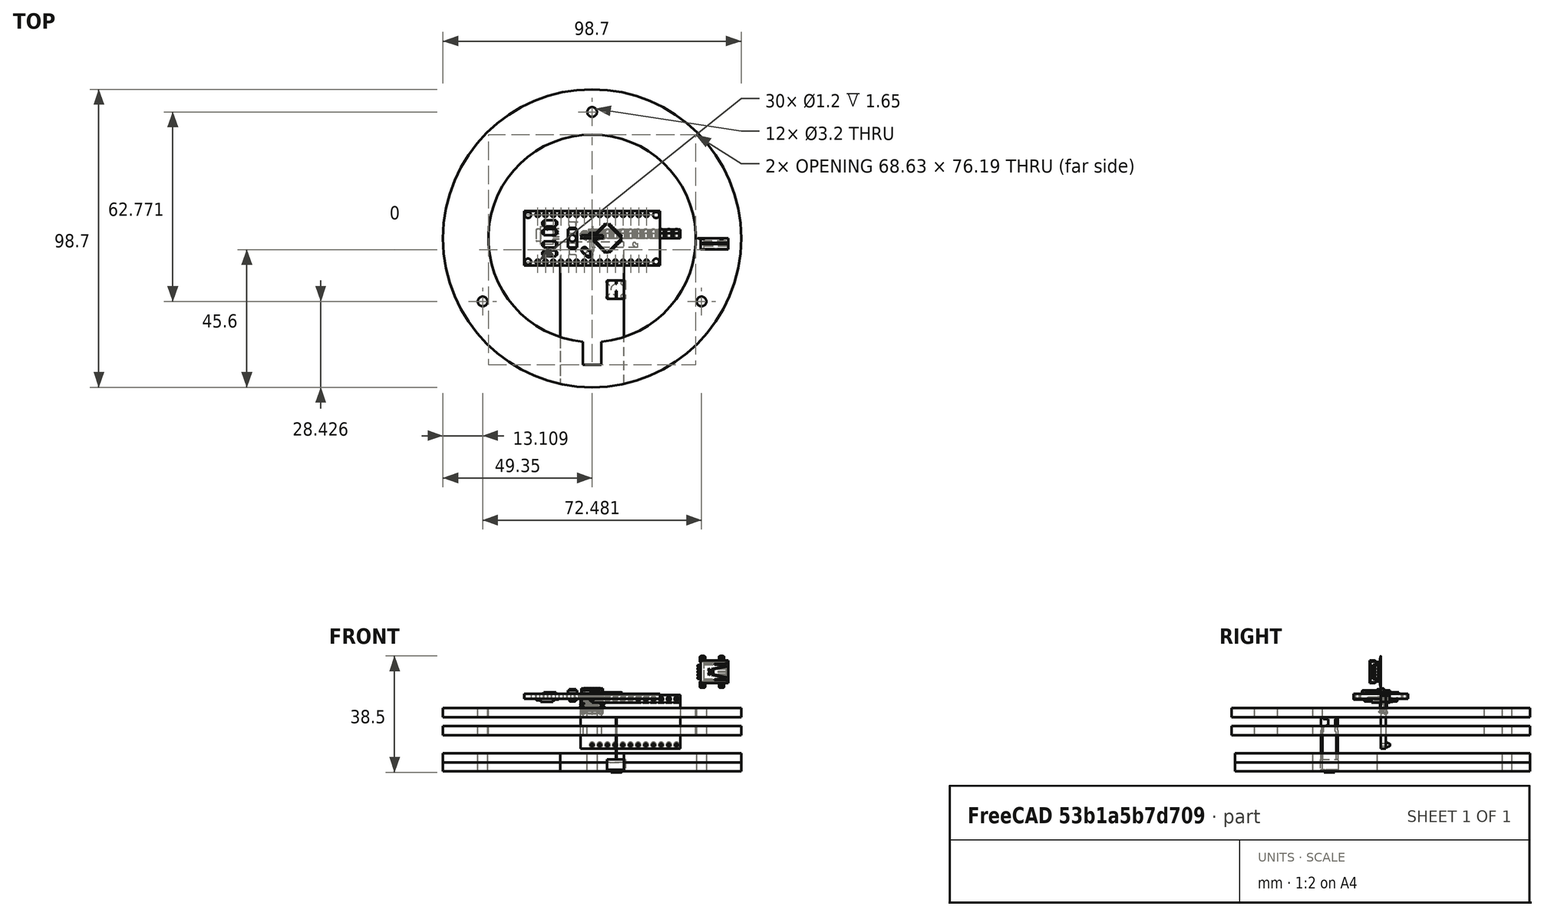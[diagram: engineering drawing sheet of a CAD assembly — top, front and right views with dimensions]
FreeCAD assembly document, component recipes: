
FREECAD ASSEMBLY — COMPONENT RECIPES ("infinity_01")

This assembly document has 81 components, labeled P0..P80 below (a component is one placed body or linked part). 6 of them carry a construction recipe — the FreeCAD feature program that regenerates the part from scratch, quoted from this document or its linked companion documents; the rest are supplied as boundary geometry only. No exploded tour is included for this assembly.
COMPONENT P0 — recipe-attached ("front_mirror_50%", modeled in this document).
Construction recipe (the document's own serialized feature program — sketch geometry with constraints, then the solid features built on it; lengths are millimeters unless a unit is written):

FEATURE [Sketcher::SketchObject] Sketch
  FullyConstrained = true
  MapMode = 5
  Support = -> [XY_Plane]
  expr: Constraints[18] = Spreadsheet.length_of_LEDS / 3.14 + 5mm + 15mm
  expr: Constraints[2] = Spreadsheet.length_of_LEDS / 3.14 + 5mm + 30mm
  expr: Constraints[3] = Spreadsheet.screw_hole_dia + 0.2mm
  sketch-geometry (8):
    g0: Circle CenterX=0 CenterY=0 CenterZ=0 NormalX=0 NormalY=0 NormalZ=1 AngleXU=0 Radius=49.3471
    g1: Circle CenterX=-36.2407 CenterY=-20.9236 CenterZ=0 NormalX=0 NormalY=0 NormalZ=1 AngleXU=0 Radius=1.6
    g2: Circle CenterX=36.2407 CenterY=-20.9236 CenterZ=0 NormalX=0 NormalY=0 NormalZ=1 AngleXU=0 Radius=1.6
    g3: Circle CenterX=0 CenterY=41.8471 CenterZ=0 NormalX=0 NormalY=0 NormalZ=1 AngleXU=0 Radius=1.6
    g4: LineSegment StartX=0 StartY=0 StartZ=0 EndX=0 EndY=41.8471 EndZ=0
    g5: LineSegment StartX=0 StartY=0 StartZ=0 EndX=36.2407 EndY=-20.9236 EndZ=0
    g6: LineSegment StartX=0 StartY=0 StartZ=0 EndX=-36.2407 EndY=-20.9236 EndZ=0
    g7: Circle CenterX=0 CenterY=0 CenterZ=0 NormalX=0 NormalY=0 NormalZ=1 AngleXU=0 Radius=41.8471
  constraints (19):
    c: Coincident(g0,g-1)
    c: PointOnObject(g3,g-2)
    c: Diameter(g0) = 98.6943
    c: Diameter(g1) = 3.2
    c: Equal(g1,g3)
    c: Equal(g1,g2)
    c: Coincident(g4,g0)
    c: Coincident(g4,g3)
    c: Coincident(g5,g0)
    c: Coincident(g5,g2)
    c: Coincident(g6,g0)
    c: Coincident(g6,g1)
    c: Equal(g6,g5)
    c: Equal(g5,g4)
    c: Angle(g5,g4) = 2.0944
    c: Angle(g4,g6) = 2.0944
    c: Coincident(g7,g0)
    c: PointOnObject(g3,g7)
    c: Diameter(g7) = 83.6943
FEATURE [PartDesign::Pad] Pad
  Direction = (1,1,1)
  Length = 3
  Length2 = 100
  Profile = -> Sketch
  Type = 0
FEATURE [PartDesign::Body] Body  label="front_mirror_50%"
  Group = -> [Sketch,Pad]
  Origin = -> Origin
  Tip = -> Pad
COMPONENT P1 — recipe-attached ("spacer01", modeled in this document).
Construction recipe (the document's own serialized feature program — sketch geometry with constraints, then the solid features built on it; lengths are millimeters unless a unit is written):

FEATURE [PartDesign::SubShapeBinder] Binder
  BindMode = 0
  ClaimChildren = false
  Context = -> Body001 [Binder.]
  Fuse = false
  MakeFace = true
  PartialLoad = false
  Relative = true
  Support = -> [Body]
  _Version = 2
FEATURE [Sketcher::SketchObject] Sketch001
  ExternalGeometry = -> [Binder]
  FullyConstrained = true
  MapMode = 5
  Placement = pos=(0,0,0) rot=(1,0,0;3.14159rad)
  Support = -> [Binder]
  expr: Constraints[8] = Spreadsheet.length_of_LEDS / 3.14 + 5mm
  sketch-geometry (10):
    g0: Circle CenterX=0 CenterY=0 CenterZ=0 NormalX=0 NormalY=0 NormalZ=1 AngleXU=0 Radius=49.3471
    g1: Circle CenterX=-36.2407 CenterY=20.9236 CenterZ=0 NormalX=0 NormalY=0 NormalZ=1 AngleXU=0 Radius=1.6
    g2: Circle CenterX=36.2407 CenterY=20.9236 CenterZ=0 NormalX=0 NormalY=0 NormalZ=1 AngleXU=0 Radius=1.6
    g3: Circle CenterX=0 CenterY=-41.8471 CenterZ=0 NormalX=0 NormalY=0 NormalZ=1 AngleXU=0 Radius=1.6
    g4: ArcOfCircle CenterX=0 CenterY=0 CenterZ=0 NormalX=0 NormalY=0 NormalZ=1 AngleXU=0 Radius=34.3471 StartAngle=1.65825 EndAngle=7.76653
    g5: LineSegment StartX=-3 StartY=41.8471 StartZ=0 EndX=3 EndY=41.8471 EndZ=0
    g6: LineSegment StartX=3 StartY=41.8471 StartZ=0 EndX=3 EndY=34.2159 EndZ=0
    g7: LineSegment StartX=-3 StartY=34.2159 StartZ=0 EndX=-3 EndY=41.8471 EndZ=0
    g8: LineSegment StartX=0 StartY=0 StartZ=0 EndX=-36.2407 EndY=20.9236 EndZ=0
    g9: LineSegment StartX=0 StartY=0 StartZ=0 EndX=0 EndY=41.8471 EndZ=0
  constraints (24):
    c: Coincident(g0,g-1)
    c: Coincident(g1,g-4)
    c: Coincident(g2,g-5)
    c: Coincident(g3,g-6)
    c: Equal(g3,g-6)
    c: Equal(g-4,g1)
    c: Equal(g-5,g2)
    c: Coincident(g4,g0)
    c: Diameter(g4) = 68.6943
    c: Coincident(g5,g6)
    c: Coincident(g7,g5)
    c: Vertical(g6)
    c: Vertical(g7)
    c: Symmetric(g5,g5,g-2)
    c: DistanceX(g5,g5) = 6
    c: Coincident(g4,g7)
    c: Coincident(g4,g6)
    c: Equal(g0,g-3)
    c: Coincident(g8,g0)
    c: Coincident(g8,g1)
    c: Coincident(g9,g0)
    c: PointOnObject(g9,g5)
    c: Vertical(g9)
    c: Equal(g8,g9)
FEATURE [PartDesign::Pad] Pad001
  Direction = (1,1,1)
  Length = 3
  Length2 = 100
  Profile = -> Sketch001
  Type = 0
FEATURE [PartDesign::Body] Body001  label="spacer01"
  Group = -> [Binder,Sketch001,Pad001]
  Origin = -> Origin001
  Tip = -> Pad001
COMPONENT P2 — recipe-attached ("bezel", modeled in this document).
Construction recipe (the document's own serialized feature program — sketch geometry with constraints, then the solid features built on it; lengths are millimeters unless a unit is written):

FEATURE [PartDesign::SubShapeBinder] Binder001
  BindMode = 0
  ClaimChildren = false
  Context = -> Body002 [Binder001.]
  Fuse = false
  MakeFace = true
  PartialLoad = false
  Relative = true
  Support = -> [Body]
  _Version = 2
FEATURE [PartDesign::SubShapeBinder] Binder002
  BindMode = 0
  ClaimChildren = false
  Context = -> Body002 [Binder002.]
  Fuse = false
  MakeFace = true
  PartialLoad = false
  Relative = true
  Support = -> [Body001]
  _Version = 2
FEATURE [Sketcher::SketchObject] Sketch002
  ExternalGeometry = -> [Binder001,Binder002]
  FullyConstrained = true
  MapMode = 5
  Placement = pos=(0,0,3) rot=(0,0,1;0rad)
  Support = -> [Binder001]
  expr: Constraints[9] = Spreadsheet.length_of_LEDS / 3.14
  sketch-geometry (5):
    g0: Circle CenterX=0 CenterY=0 CenterZ=0 NormalX=0 NormalY=0 NormalZ=1 AngleXU=0 Radius=49.3471
    g1: Circle CenterX=0 CenterY=0 CenterZ=0 NormalX=0 NormalY=0 NormalZ=1 AngleXU=0 Radius=31.8471
    g2: Circle CenterX=-36.2407 CenterY=-20.9236 CenterZ=0 NormalX=0 NormalY=0 NormalZ=1 AngleXU=0 Radius=1.6
    g3: Circle CenterX=0 CenterY=41.8471 CenterZ=0 NormalX=0 NormalY=0 NormalZ=1 AngleXU=0 Radius=1.6
    g4: Circle CenterX=36.2407 CenterY=-20.9236 CenterZ=0 NormalX=0 NormalY=0 NormalZ=1 AngleXU=0 Radius=1.6
  constraints (10):
    c: Coincident(g0,g-1)
    c: Coincident(g1,g0)
    c: Coincident(g2,g-6)
    c: Coincident(g3,g-4)
    c: Coincident(g4,g-5)
    c: Equal(g-5,g4)
    c: Equal(g2,g-6)
    c: Equal(g-4,g3)
    c: Equal(g0,g-3)
    c: Diameter(g1) = 63.6943
FEATURE [PartDesign::Pad] Pad002
  Direction = (1,1,1)
  Length = 3
  Length2 = 100
  Profile = -> Sketch002
  Type = 0
FEATURE [PartDesign::Body] Body002  label="bezel"
  Group = -> [Binder001,Sketch002,Binder002,Pad002]
  Origin = -> Origin002
  Tip = -> Pad002
COMPONENT P3 — geometry summary ("spacer02"; no construction recipe available for this part):
  bounding box: 98.7 x 98.7 x 3.0 mm
  tessellated surface: 2,532 triangles
  volume: 11624 mm^3 (40% of its bounding box)
  symmetry: 2-fold rotationally symmetric about the y axis; mirror-symmetric across its x mid-plane, z mid-plane
COMPONENT P4 — geometry summary ("spacer03"; no construction recipe available for this part):
  bounding box: 98.7 x 98.7 x 3.0 mm
  tessellated surface: 2,532 triangles
  volume: 11624 mm^3 (40% of its bounding box)
  symmetry: 2-fold rotationally symmetric about the y axis; mirror-symmetric across its x mid-plane, z mid-plane
COMPONENT P5 — recipe-attached ("back_mirror_100%", modeled in this document).
Construction recipe (the document's own serialized feature program — sketch geometry with constraints, then the solid features built on it; lengths are millimeters unless a unit is written):

FEATURE [PartDesign::SubShapeBinder] Binder007
  BindMode = 0
  ClaimChildren = false
  Context = -> Body005 [Binder007.]
  Fuse = false
  MakeFace = true
  PartialLoad = false
  Relative = true
  Support = -> [Body009]
  _Version = 2
FEATURE [Sketcher::SketchObject] Sketch003
  ExternalGeometry = -> [Binder007]
  FullyConstrained = true
  MapMode = 5
  Placement = pos=(0,0,-6) rot=(1,0,0;3.14159rad)
  Support = -> [Binder007]
  sketch-geometry (8):
    g0: Circle CenterX=0 CenterY=0 CenterZ=0 NormalX=0 NormalY=0 NormalZ=1 AngleXU=0 Radius=49.3471
    g1: Circle CenterX=-36.2407 CenterY=20.9236 CenterZ=0 NormalX=0 NormalY=0 NormalZ=1 AngleXU=0 Radius=1.6
    g2: Circle CenterX=36.2407 CenterY=20.9236 CenterZ=0 NormalX=0 NormalY=0 NormalZ=1 AngleXU=0 Radius=1.6
    g3: Circle CenterX=0 CenterY=-41.8471 CenterZ=0 NormalX=0 NormalY=0 NormalZ=1 AngleXU=0 Radius=1.6
    g4: LineSegment StartX=3 StartY=34.2159 StartZ=0 EndX=-3 EndY=34.2159 EndZ=0
    g5: LineSegment StartX=-3 StartY=34.2159 StartZ=0 EndX=-3 EndY=41.8471 EndZ=0
    g6: LineSegment StartX=-3 StartY=41.8471 StartZ=0 EndX=3 EndY=41.8471 EndZ=0
    g7: LineSegment StartX=3 StartY=41.8471 StartZ=0 EndX=3 EndY=34.2159 EndZ=0
  constraints (18):
    c: Coincident(g0,g-1)
    c: Coincident(g4,g5)
    c: Coincident(g5,g6)
    c: Coincident(g6,g7)
    c: Coincident(g7,g4)
    c: Horizontal(g4)
    c: Horizontal(g6)
    c: Vertical(g5)
    c: Vertical(g7)
    c: Equal(g-3,g0)
    c: Equal(g-4,g1)
    c: Coincident(g1,g-4)
    c: Coincident(g2,g-5)
    c: Equal(g-5,g2)
    c: Coincident(g3,g-6)
    c: Equal(g-6,g3)
    c: Coincident(g5,g-7)
    c: Coincident(g4,g-8)
FEATURE [PartDesign::Pad] Pad003
  Direction = (1,1,1)
  Length = 3
  Length2 = 100
  Profile = -> Sketch003
  Type = 0
FEATURE [PartDesign::Body] Body005  label="back_mirror_100%"
  Group = -> [Sketch003,Pad003,Binder007]
  Origin = -> Origin005
  Placement = pos=(0,0,-6) rot=(0,0,1;0rad)
  Tip = -> Pad003
COMPONENT P6 — recipe-attached ("arduino_micro_back001", modeled in this document).
Construction recipe (the document's own serialized feature program — sketch geometry with constraints, then the solid features built on it; lengths are millimeters unless a unit is written):

FEATURE [PartDesign::SubShapeBinder] Binder004
  BindMode = 0
  ClaimChildren = false
  Context = -> Body006 [Binder004.]
  Fuse = false
  MakeFace = true
  PartialLoad = false
  Relative = true
  Support = -> [Body005]
  _Version = 2
FEATURE [Sketcher::SketchObject] Sketch004
  ExternalGeometry = -> [Binder004]
  FullyConstrained = true
  MapMode = 5
  Placement = pos=(0,0,-15) rot=(1,0,0;3.14159rad)
  Support = -> [Binder004]
  expr: Constraints[6] = Spreadsheet.width
  expr: Constraints[9] = Spreadsheet.Length
  sketch-geometry (7):
    g0: ArcOfCircle CenterX=0 CenterY=0 CenterZ=0 NormalX=0 NormalY=0 NormalZ=1 AngleXU=0 Radius=49.3471 StartAngle=1.78521 EndAngle=7.63956
    g1: LineSegment StartX=10.5 StartY=48.2171 StartZ=0 EndX=10.5 EndY=1.21711 EndZ=0
    g2: LineSegment StartX=10.5 StartY=1.21711 StartZ=0 EndX=-10.5 EndY=1.21711 EndZ=0
    g3: LineSegment StartX=-10.5 StartY=1.21711 StartZ=0 EndX=-10.5 EndY=48.2171 EndZ=0
    g4: Circle CenterX=-36.2407 CenterY=20.9236 CenterZ=0 NormalX=0 NormalY=0 NormalZ=1 AngleXU=0 Radius=1.6
    g5: Circle CenterX=36.2407 CenterY=20.9236 CenterZ=0 NormalX=0 NormalY=0 NormalZ=1 AngleXU=0 Radius=1.6
    g6: Circle CenterX=0 CenterY=-41.8471 CenterZ=0 NormalX=0 NormalY=0 NormalZ=1 AngleXU=0 Radius=1.6
  constraints (17):
    c: Coincident(g0,g-1)
    c: Coincident(g1,g2)
    c: Coincident(g2,g3)
    c: Vertical(g1)
    c: Vertical(g3)
    c: Symmetric(g2,g1,g-2)
    c: DistanceX(g2,g2) = 21
    c: Coincident(g0,g3)
    c: Coincident(g0,g1)
    c: Distance(g3) = 47
    c: Equal(g0,g-3)
    c: Coincident(g4,g-4)
    c: Coincident(g5,g-5)
    c: Coincident(g6,g-6)
    c: Equal(g6,g-6)
    c: Equal(g-4,g4)
    c: Equal(g-5,g5)
FEATURE [PartDesign::Pad] Pad004
  Direction = (1,1,1)
  Length = 3
  Length2 = 100
  Profile = -> Sketch004
  Type = 0
FEATURE [PartDesign::Body] Body006  label="arduino_micro_back001"
  Group = -> [Binder004,Sketch004,Pad004]
  Origin = -> Origin006
  Tip = -> Pad004
COMPONENT P7 — geometry summary ("arduino_micro_back002"; no construction recipe available for this part):
  bounding box: 98.7 x 97.6 x 3.0 mm
  tessellated surface: 2,004 triangles
  volume: 19870 mm^3 (69% of its bounding box)
  symmetry: mirror-symmetric across its x mid-plane, z mid-plane
COMPONENT P8 — geometry summary ("spacer04"; no construction recipe available for this part):
  bounding box: 98.7 x 98.7 x 3.0 mm
  tessellated surface: 2,532 triangles
  volume: 11624 mm^3 (40% of its bounding box)
  symmetry: 2-fold rotationally symmetric about the y axis; mirror-symmetric across its x mid-plane, z mid-plane
COMPONENT P9 — geometry summary ("arduino_micro_back003"; no construction recipe available for this part):
  bounding box: 98.7 x 97.6 x 3.0 mm
  tessellated surface: 2,004 triangles
  volume: 19870 mm^3 (69% of its bounding box)
  symmetry: mirror-symmetric across its x mid-plane, z mid-plane
COMPONENT P10 — recipe-attached ("back", modeled in this document).
Construction recipe (the document's own serialized feature program — sketch geometry with constraints, then the solid features built on it; lengths are millimeters unless a unit is written):

FEATURE [PartDesign::SubShapeBinder] Binder005
  BindMode = 0
  ClaimChildren = false
  Context = -> Body011 [Binder005.]
  Fuse = false
  MakeFace = true
  PartialLoad = false
  Relative = true
  Support = -> [Body010]
  _Version = 2
FEATURE [PartDesign::SubShapeBinder] Binder006
  BindMode = 0
  ClaimChildren = false
  Context = -> Body011 [Binder006.]
  Fuse = false
  MakeFace = true
  PartialLoad = false
  Relative = true
  Support = -> [Solid105]
  _Version = 2
FEATURE [Sketcher::SketchObject] Sketch005
  ExternalGeometry = -> [Binder005,Binder006]
  FullyConstrained = true
  MapMode = 5
  Placement = pos=(0,0,-24) rot=(1,0,0;3.14159rad)
  Support = -> [Binder005]
  sketch-geometry (5):
    g0: Circle CenterX=0 CenterY=0 CenterZ=0 NormalX=0 NormalY=0 NormalZ=1 AngleXU=0 Radius=49.3471
    g1: Circle CenterX=-36.2407 CenterY=20.9236 CenterZ=0 NormalX=0 NormalY=0 NormalZ=1 AngleXU=0 Radius=1.6
    g2: Circle CenterX=36.2407 CenterY=20.9236 CenterZ=0 NormalX=0 NormalY=0 NormalZ=1 AngleXU=0 Radius=1.6
    g3: Circle CenterX=0 CenterY=-41.8471 CenterZ=0 NormalX=0 NormalY=0 NormalZ=1 AngleXU=0 Radius=1.6
    g4: Circle CenterX=8 CenterY=17 CenterZ=0 NormalX=0 NormalY=0 NormalZ=1 AngleXU=0 Radius=5
  constraints (10):
    c: Coincident(g0,g-1)
    c: Coincident(g2,g-5)
    c: Coincident(g3,g-6)
    c: Equal(g-6,g3)
    c: Equal(g1,g-4)
    c: Coincident(g1,g-4)
    c: Equal(g-5,g2)
    c: Equal(g0,g-3)
    c: Coincident(g-7,g4)
    c: Diameter(g4) = 10
FEATURE [PartDesign::Pad] Pad005
  Direction = (1,1,1)
  Length = 3
  Length2 = 100
  Profile = -> Sketch005
  Type = 0
FEATURE [PartDesign::Body] Body011  label="back"
  Group = -> [Binder005,Sketch005,Binder006,Pad005]
  Origin = -> Origin011
  Tip = -> Pad005
COMPONENT P11 — geometry summary ("Component3:2"; no construction recipe available for this part):
  bounding box: 0.9 x 0.6 x 0.3 mm
  tessellated surface: 80 triangles
  volume: 0 mm^3 (64% of its bounding box)
  symmetry: mirror-symmetric across its x mid-plane
COMPONENT P12 — geometry summary ("Component3:3"; no construction recipe available for this part):
  bounding box: 0.9 x 0.6 x 0.3 mm
  tessellated surface: 80 triangles
  volume: 0 mm^3 (64% of its bounding box)
  symmetry: mirror-symmetric across its x mid-plane
COMPONENT P13 — geometry summary ("Component3:4"; no construction recipe available for this part):
  bounding box: 0.9 x 0.6 x 0.3 mm
  tessellated surface: 80 triangles
  volume: 0 mm^3 (64% of its bounding box)
  symmetry: mirror-symmetric across its x mid-plane
COMPONENT P14 — geometry summary ("Component3:5"; no construction recipe available for this part):
  bounding box: 0.9 x 0.6 x 0.3 mm
  tessellated surface: 80 triangles
  volume: 0 mm^3 (64% of its bounding box)
  symmetry: mirror-symmetric across its x mid-plane
COMPONENT P15 — geometry summary ("Component3:6"; no construction recipe available for this part):
  bounding box: 0.9 x 0.6 x 0.3 mm
  tessellated surface: 80 triangles
  volume: 0 mm^3 (64% of its bounding box)
  symmetry: mirror-symmetric across its x mid-plane
COMPONENT P16 — geometry summary ("Component3:7"; no construction recipe available for this part):
  bounding box: 0.9 x 0.6 x 0.3 mm
  tessellated surface: 80 triangles
  volume: 0 mm^3 (64% of its bounding box)
  symmetry: mirror-symmetric across its x mid-plane
COMPONENT P17 — geometry summary ("Component3:8"; no construction recipe available for this part):
  bounding box: 0.9 x 0.6 x 0.3 mm
  tessellated surface: 80 triangles
  volume: 0 mm^3 (64% of its bounding box)
  symmetry: mirror-symmetric across its x mid-plane
COMPONENT P18 — geometry summary ("Component3:9"; no construction recipe available for this part):
  bounding box: 0.9 x 0.6 x 0.3 mm
  tessellated surface: 80 triangles
  volume: 0 mm^3 (64% of its bounding box)
  symmetry: mirror-symmetric across its x mid-plane
COMPONENT P19 — geometry summary ("Component3:10"; no construction recipe available for this part):
  bounding box: 0.9 x 0.6 x 0.3 mm
  tessellated surface: 80 triangles
  volume: 0 mm^3 (64% of its bounding box)
  symmetry: mirror-symmetric across its x mid-plane
COMPONENT P20 — geometry summary ("Component3:11"; no construction recipe available for this part):
  bounding box: 0.9 x 0.6 x 0.3 mm
  tessellated surface: 80 triangles
  volume: 0 mm^3 (64% of its bounding box)
  symmetry: mirror-symmetric across its x mid-plane
COMPONENT P21 — geometry summary ("Component3:12"; no construction recipe available for this part):
  bounding box: 0.9 x 0.6 x 0.3 mm
  tessellated surface: 80 triangles
  volume: 0 mm^3 (64% of its bounding box)
  symmetry: mirror-symmetric across its x mid-plane
COMPONENT P22 — geometry summary ("Component3:13"; no construction recipe available for this part):
  bounding box: 0.9 x 0.6 x 0.3 mm
  tessellated surface: 80 triangles
  volume: 0 mm^3 (64% of its bounding box)
  symmetry: mirror-symmetric across its x mid-plane
COMPONENT P23 — geometry summary ("Component3:14"; no construction recipe available for this part):
  bounding box: 0.9 x 0.6 x 0.3 mm
  tessellated surface: 80 triangles
  volume: 0 mm^3 (64% of its bounding box)
  symmetry: mirror-symmetric across its x mid-plane
COMPONENT P24 — geometry summary ("Component3:15"; no construction recipe available for this part):
  bounding box: 0.9 x 0.6 x 0.3 mm
  tessellated surface: 80 triangles
  volume: 0 mm^3 (64% of its bounding box)
  symmetry: mirror-symmetric across its x mid-plane
COMPONENT P25 — geometry summary ("Component3:16"; no construction recipe available for this part):
  bounding box: 0.9 x 0.6 x 0.3 mm
  tessellated surface: 80 triangles
  volume: 0 mm^3 (64% of its bounding box)
  symmetry: mirror-symmetric across its x mid-plane
COMPONENT P26 — geometry summary ("Component3(Mirror):2"; no construction recipe available for this part):
  bounding box: 0.9 x 0.6 x 0.3 mm
  tessellated surface: 80 triangles
  volume: 0 mm^3 (64% of its bounding box)
  symmetry: mirror-symmetric across its x mid-plane
COMPONENT P27 — geometry summary ("Component3(Mirror):3"; no construction recipe available for this part):
  bounding box: 0.9 x 0.6 x 0.3 mm
  tessellated surface: 80 triangles
  volume: 0 mm^3 (64% of its bounding box)
  symmetry: mirror-symmetric across its x mid-plane
COMPONENT P28 — geometry summary ("Component3(Mirror):4"; no construction recipe available for this part):
  bounding box: 0.9 x 0.6 x 0.3 mm
  tessellated surface: 80 triangles
  volume: 0 mm^3 (64% of its bounding box)
  symmetry: mirror-symmetric across its x mid-plane
COMPONENT P29 — geometry summary ("Component3(Mirror):5"; no construction recipe available for this part):
  bounding box: 0.9 x 0.6 x 0.3 mm
  tessellated surface: 80 triangles
  volume: 0 mm^3 (64% of its bounding box)
  symmetry: mirror-symmetric across its x mid-plane
COMPONENT P30 — geometry summary ("Component3(Mirror):6"; no construction recipe available for this part):
  bounding box: 0.9 x 0.6 x 0.3 mm
  tessellated surface: 80 triangles
  volume: 0 mm^3 (64% of its bounding box)
  symmetry: mirror-symmetric across its x mid-plane
COMPONENT P31 — geometry summary ("Component3(Mirror):7"; no construction recipe available for this part):
  bounding box: 0.9 x 0.6 x 0.3 mm
  tessellated surface: 80 triangles
  volume: 0 mm^3 (64% of its bounding box)
  symmetry: mirror-symmetric across its x mid-plane
COMPONENT P32 — geometry summary ("Component3(Mirror):8"; no construction recipe available for this part):
  bounding box: 0.9 x 0.6 x 0.3 mm
  tessellated surface: 80 triangles
  volume: 0 mm^3 (64% of its bounding box)
  symmetry: mirror-symmetric across its x mid-plane
COMPONENT P33 — geometry summary ("Component3(Mirror):9"; no construction recipe available for this part):
  bounding box: 0.9 x 0.6 x 0.3 mm
  tessellated surface: 80 triangles
  volume: 0 mm^3 (64% of its bounding box)
  symmetry: mirror-symmetric across its x mid-plane
COMPONENT P34 — geometry summary ("Component3(Mirror):10"; no construction recipe available for this part):
  bounding box: 0.9 x 0.6 x 0.3 mm
  tessellated surface: 80 triangles
  volume: 0 mm^3 (64% of its bounding box)
  symmetry: mirror-symmetric across its x mid-plane
COMPONENT P35 — geometry summary ("Component3(Mirror):11"; no construction recipe available for this part):
  bounding box: 0.9 x 0.6 x 0.3 mm
  tessellated surface: 80 triangles
  volume: 0 mm^3 (64% of its bounding box)
  symmetry: mirror-symmetric across its x mid-plane
COMPONENT P36 — geometry summary ("Component3(Mirror):12"; no construction recipe available for this part):
  bounding box: 0.9 x 0.6 x 0.3 mm
  tessellated surface: 80 triangles
  volume: 0 mm^3 (64% of its bounding box)
  symmetry: mirror-symmetric across its x mid-plane
COMPONENT P37 — geometry summary ("Component3(Mirror):13"; no construction recipe available for this part):
  bounding box: 0.9 x 0.6 x 0.3 mm
  tessellated surface: 80 triangles
  volume: 0 mm^3 (64% of its bounding box)
  symmetry: mirror-symmetric across its x mid-plane
COMPONENT P38 — geometry summary ("Component3(Mirror):14"; no construction recipe available for this part):
  bounding box: 0.9 x 0.6 x 0.3 mm
  tessellated surface: 80 triangles
  volume: 0 mm^3 (64% of its bounding box)
  symmetry: mirror-symmetric across its x mid-plane
COMPONENT P39 — geometry summary ("Component3(Mirror):15"; no construction recipe available for this part):
  bounding box: 0.9 x 0.6 x 0.3 mm
  tessellated surface: 80 triangles
  volume: 0 mm^3 (64% of its bounding box)
  symmetry: mirror-symmetric across its x mid-plane
COMPONENT P40 — geometry summary ("Component3(Mirror):16"; no construction recipe available for this part):
  bounding box: 0.9 x 0.6 x 0.3 mm
  tessellated surface: 80 triangles
  volume: 0 mm^3 (64% of its bounding box)
  symmetry: mirror-symmetric across its x mid-plane
COMPONENT P41 — geometry summary ("Component5:3"; no construction recipe available for this part):
  bounding box: 0.7 x 0.5 x 0.2 mm
  tessellated surface: 76 triangles
  volume: 0 mm^3 (64% of its bounding box)
  symmetry: mirror-symmetric across its y mid-plane
COMPONENT P42 — geometry summary ("Component5:4"; no construction recipe available for this part):
  bounding box: 0.7 x 0.5 x 0.2 mm
  tessellated surface: 76 triangles
  volume: 0 mm^3 (64% of its bounding box)
  symmetry: mirror-symmetric across its y mid-plane
COMPONENT P43 — geometry summary ("Component5:5"; no construction recipe available for this part):
  bounding box: 0.7 x 0.5 x 0.2 mm
  tessellated surface: 76 triangles
  volume: 0 mm^3 (64% of its bounding box)
  symmetry: mirror-symmetric across its y mid-plane
COMPONENT P44 — geometry summary ("Component5(Mirror):2"; no construction recipe available for this part):
  bounding box: 0.7 x 0.5 x 0.2 mm
  tessellated surface: 76 triangles
  volume: 0 mm^3 (64% of its bounding box)
  symmetry: mirror-symmetric across its y mid-plane
COMPONENT P45 — geometry summary ("Component5(Mirror):3"; no construction recipe available for this part):
  bounding box: 0.7 x 0.5 x 0.2 mm
  tessellated surface: 76 triangles
  volume: 0 mm^3 (64% of its bounding box)
  symmetry: mirror-symmetric across its y mid-plane
COMPONENT P46 — geometry summary ("Component5(Mirror):4"; no construction recipe available for this part):
  bounding box: 0.7 x 0.5 x 0.2 mm
  tessellated surface: 76 triangles
  volume: 0 mm^3 (64% of its bounding box)
  symmetry: mirror-symmetric across its y mid-plane
COMPONENT P47 — geometry summary ("Component5:7"; no construction recipe available for this part):
  bounding box: 0.7 x 0.5 x 0.2 mm
  tessellated surface: 76 triangles
  volume: 0 mm^3 (64% of its bounding box)
  symmetry: mirror-symmetric across its y mid-plane
COMPONENT P48 — geometry summary ("Component5:8"; no construction recipe available for this part):
  bounding box: 0.7 x 0.5 x 0.2 mm
  tessellated surface: 76 triangles
  volume: 0 mm^3 (64% of its bounding box)
  symmetry: mirror-symmetric across its y mid-plane
COMPONENT P49 — geometry summary ("Component5:9"; no construction recipe available for this part):
  bounding box: 0.7 x 0.5 x 0.2 mm
  tessellated surface: 76 triangles
  volume: 0 mm^3 (64% of its bounding box)
  symmetry: mirror-symmetric across its y mid-plane
COMPONENT P50 — geometry summary ("Component5:10"; no construction recipe available for this part):
  bounding box: 0.7 x 0.5 x 0.2 mm
  tessellated surface: 76 triangles
  volume: 0 mm^3 (64% of its bounding box)
  symmetry: mirror-symmetric across its y mid-plane
COMPONENT P51 — geometry summary ("Component5(Mirror) (1):2"; no construction recipe available for this part):
  bounding box: 0.7 x 0.5 x 0.2 mm
  tessellated surface: 76 triangles
  volume: 0 mm^3 (64% of its bounding box)
  symmetry: mirror-symmetric across its y mid-plane
COMPONENT P52 — geometry summary ("Component5(Mirror) (1):3"; no construction recipe available for this part):
  bounding box: 0.7 x 0.5 x 0.2 mm
  tessellated surface: 76 triangles
  volume: 0 mm^3 (64% of its bounding box)
  symmetry: mirror-symmetric across its y mid-plane
COMPONENT P53 — geometry summary ("Component5(Mirror) (1):4"; no construction recipe available for this part):
  bounding box: 0.7 x 0.5 x 0.2 mm
  tessellated surface: 76 triangles
  volume: 0 mm^3 (64% of its bounding box)
  symmetry: mirror-symmetric across its y mid-plane
COMPONENT P54 — geometry summary ("NAUO37"; no construction recipe available for this part):
  bounding box: 11.9 x 1.7 x 1.7 mm
  tessellated surface: 3,844 triangles
  volume: 8 mm^3 (25% of its bounding box)
  symmetry: revolution-symmetric about the y axis through its bounding-box center; mirror-symmetric across its x mid-plane, z mid-plane
COMPONENT P55 — geometry summary ("NAUO38"; no construction recipe available for this part):
  bounding box: 11.9 x 1.7 x 1.7 mm
  tessellated surface: 3,844 triangles
  volume: 8 mm^3 (25% of its bounding box)
  symmetry: revolution-symmetric about the y axis through its bounding-box center; mirror-symmetric across its x mid-plane, z mid-plane
COMPONENT P56 — geometry summary ("NAUO39"; no construction recipe available for this part):
  bounding box: 11.9 x 1.7 x 1.7 mm
  tessellated surface: 3,844 triangles
  volume: 8 mm^3 (25% of its bounding box)
  symmetry: revolution-symmetric about the y axis through its bounding-box center; mirror-symmetric across its x mid-plane, z mid-plane
COMPONENT P57 — geometry summary ("NAUO40"; no construction recipe available for this part):
  bounding box: 11.9 x 1.7 x 1.7 mm
  tessellated surface: 3,844 triangles
  volume: 8 mm^3 (25% of its bounding box)
  symmetry: revolution-symmetric about the y axis through its bounding-box center; mirror-symmetric across its x mid-plane, z mid-plane
COMPONENT P58 — geometry summary ("NAUO41"; no construction recipe available for this part):
  bounding box: 11.9 x 1.7 x 1.7 mm
  tessellated surface: 3,844 triangles
  volume: 8 mm^3 (25% of its bounding box)
  symmetry: revolution-symmetric about the y axis through its bounding-box center; mirror-symmetric across its x mid-plane, z mid-plane
COMPONENT P59 — geometry summary ("NAUO42"; no construction recipe available for this part):
  bounding box: 11.9 x 1.7 x 1.7 mm
  tessellated surface: 3,844 triangles
  volume: 8 mm^3 (25% of its bounding box)
  symmetry: revolution-symmetric about the y axis through its bounding-box center; mirror-symmetric across its x mid-plane, z mid-plane
COMPONENT P60 — geometry summary ("NAUO43"; no construction recipe available for this part):
  bounding box: 11.9 x 1.7 x 1.7 mm
  tessellated surface: 3,844 triangles
  volume: 8 mm^3 (25% of its bounding box)
  symmetry: revolution-symmetric about the y axis through its bounding-box center; mirror-symmetric across its x mid-plane, z mid-plane
COMPONENT P61 — geometry summary ("NAUO44"; no construction recipe available for this part):
  bounding box: 11.9 x 1.7 x 1.7 mm
  tessellated surface: 3,844 triangles
  volume: 8 mm^3 (25% of its bounding box)
  symmetry: revolution-symmetric about the y axis through its bounding-box center; mirror-symmetric across its x mid-plane, z mid-plane
COMPONENT P62 — geometry summary ("NAUO45"; no construction recipe available for this part):
  bounding box: 11.9 x 1.7 x 1.7 mm
  tessellated surface: 3,844 triangles
  volume: 8 mm^3 (25% of its bounding box)
  symmetry: revolution-symmetric about the y axis through its bounding-box center; mirror-symmetric across its x mid-plane, z mid-plane
COMPONENT P63 — geometry summary ("NAUO46"; no construction recipe available for this part):
  bounding box: 11.9 x 1.7 x 1.7 mm
  tessellated surface: 3,844 triangles
  volume: 8 mm^3 (25% of its bounding box)
  symmetry: revolution-symmetric about the y axis through its bounding-box center; mirror-symmetric across its x mid-plane, z mid-plane
COMPONENT P64 — geometry summary ("NAUO47"; no construction recipe available for this part):
  bounding box: 11.9 x 1.7 x 1.7 mm
  tessellated surface: 3,844 triangles
  volume: 8 mm^3 (25% of its bounding box)
  symmetry: revolution-symmetric about the y axis through its bounding-box center; mirror-symmetric across its x mid-plane, z mid-plane
COMPONENT P65 — geometry summary ("NAUO31"; no construction recipe available for this part):
  bounding box: 4.4 x 1.3 x 0.2 mm
  tessellated surface: 172 triangles
  volume: 0 mm^3 (19% of its bounding box)
  symmetry: mirror-symmetric across its x mid-plane
COMPONENT P66 — geometry summary ("NAUO32"; no construction recipe available for this part):
  bounding box: 4.4 x 1.3 x 0.2 mm
  tessellated surface: 172 triangles
  volume: 0 mm^3 (19% of its bounding box)
  symmetry: mirror-symmetric across its x mid-plane
COMPONENT P67 — geometry summary ("NAUO33"; no construction recipe available for this part):
  bounding box: 4.4 x 1.3 x 0.2 mm
  tessellated surface: 172 triangles
  volume: 0 mm^3 (19% of its bounding box)
  symmetry: mirror-symmetric across its x mid-plane
COMPONENT P68 — geometry summary ("NAUO34"; no construction recipe available for this part):
  bounding box: 4.4 x 1.3 x 0.2 mm
  tessellated surface: 172 triangles
  volume: 0 mm^3 (19% of its bounding box)
  symmetry: mirror-symmetric across its x mid-plane
COMPONENT P69 — geometry summary ("NAUO6"; no construction recipe available for this part):
  bounding box: 4.0 x 1.8 x 1.7 mm
  tessellated surface: 1,768 triangles
  volume: 10 mm^3 (81% of its bounding box)
  symmetry: mirror-symmetric across its z mid-plane
COMPONENT P70 — geometry summary ("NAUO7"; no construction recipe available for this part):
  bounding box: 30.5 x 11.9 x 2.5 mm
  tessellated surface: 50,788 triangles
  volume: 272 mm^3 (30% of its bounding box)
  symmetry: 2-fold rotationally symmetric about the y axis; mirror-symmetric across its x mid-plane, z mid-plane
COMPONENT P71 — geometry summary ("NAUO13"; no construction recipe available for this part):
  bounding box: 2.4 x 1.0 x 0.6 mm
  tessellated surface: 592 triangles
  volume: 1 mm^3 (54% of its bounding box)
  symmetry: 2-fold rotationally symmetric about the y axis; mirror-symmetric across its x mid-plane, z mid-plane
COMPONENT P72 — geometry summary ("NAUO16"; no construction recipe available for this part):
  bounding box: 2.4 x 1.0 x 0.6 mm
  tessellated surface: 652 triangles
  volume: 1 mm^3 (54% of its bounding box)
  symmetry: 2-fold rotationally symmetric about the y axis; mirror-symmetric across its x mid-plane, z mid-plane
COMPONENT P73 — geometry summary ("NAUO18"; no construction recipe available for this part):
  bounding box: 2.8 x 1.0 x 0.9 mm
  tessellated surface: 1,662 triangles
  volume: 1 mm^3 (51% of its bounding box)
  symmetry: mirror-symmetric across its x mid-plane, z mid-plane
COMPONENT P74 — geometry summary ("NAUO19"; no construction recipe available for this part):
  bounding box: 2.8 x 1.0 x 0.9 mm
  tessellated surface: 1,662 triangles
  volume: 1 mm^3 (51% of its bounding box)
  symmetry: mirror-symmetric across its x mid-plane, z mid-plane
COMPONENT P75 — geometry summary ("NAUO20"; no construction recipe available for this part):
  bounding box: 2.8 x 1.0 x 0.9 mm
  tessellated surface: 1,662 triangles
  volume: 1 mm^3 (51% of its bounding box)
  symmetry: mirror-symmetric across its x mid-plane, z mid-plane
COMPONENT P76 — geometry summary ("NAUO21"; no construction recipe available for this part):
  bounding box: 2.8 x 1.0 x 0.9 mm
  tessellated surface: 1,662 triangles
  volume: 1 mm^3 (51% of its bounding box)
  symmetry: mirror-symmetric across its x mid-plane, z mid-plane
COMPONENT P77 — geometry summary ("NAUO22"; no construction recipe available for this part):
  bounding box: 2.8 x 1.0 x 0.9 mm
  tessellated surface: 1,662 triangles
  volume: 1 mm^3 (51% of its bounding box)
  symmetry: mirror-symmetric across its x mid-plane, z mid-plane
COMPONENT P78 — geometry summary ("NAUO23"; no construction recipe available for this part):
  bounding box: 2.8 x 1.0 x 0.9 mm
  tessellated surface: 1,662 triangles
  volume: 1 mm^3 (51% of its bounding box)
  symmetry: mirror-symmetric across its x mid-plane, z mid-plane
COMPONENT P79 — geometry summary ("NAUO26"; no construction recipe available for this part):
  bounding box: 2.3 x 0.8 x 0.7 mm
  tessellated surface: 1,528 triangles
  volume: 1 mm^3 (54% of its bounding box)
  symmetry: 2-fold rotationally symmetric about the y axis; mirror-symmetric across its x mid-plane, z mid-plane
COMPONENT P80 — geometry summary ("NAUO27"; no construction recipe available for this part):
  bounding box: 2.3 x 0.8 x 0.7 mm
  tessellated surface: 1,528 triangles
  volume: 1 mm^3 (54% of its bounding box)
  symmetry: 2-fold rotationally symmetric about the y axis; mirror-symmetric across its x mid-plane, z mid-plane
PROVENANCE & LICENSES
A FreeCAD (.FCStd) document from a public repository crawl; recipes are the document's own serialized feature recipes (and, for linked parts, companion documents' recipes).
License: gpl-3.0.
